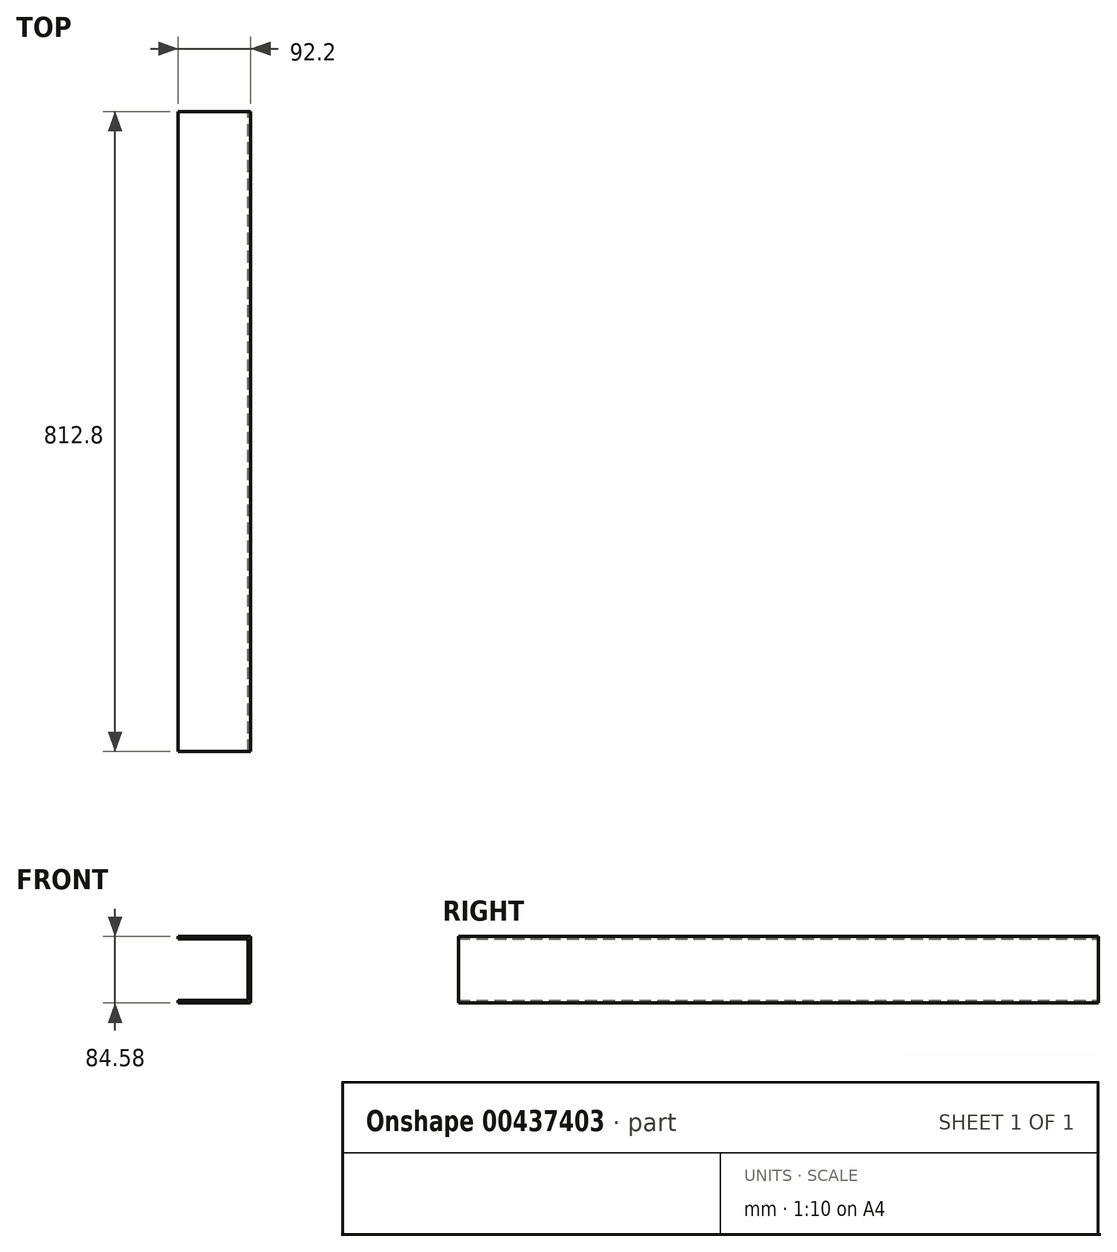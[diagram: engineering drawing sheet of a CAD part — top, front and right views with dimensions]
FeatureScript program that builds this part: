
annotation { "Feature Type Name" : "Feature", "Feature Type Description" : "" }
export const myFeature = defineFeature(function(context is Context, id is Id, definition is map)
    precondition{}
    {
        {
            var Q0;
            Q0=qCreatedBy(makeId("Right.planeOp"),FACE);
            cPlane(context, id + "F0", {"entities" : qUnion([Q0]), "cplaneType" : CPlaneType.OFFSET, "offset" : 457.2 * mm, "width" : 152.4 * mm, "height" : 152.4 * mm});
        }
        {
            var Q0;
            Q0=qCreatedBy(makeId("Front.planeOp"),FACE);
            var sketch = newSketch(context, id + "F1", { "sketchPlane" : qUnion([Q0])});
            skLineSegment(sketch, "E0", {"start": v(263.4, 52.83) * mm, "end": v(355.6, 52.83) * mm});
            skLineSegment(sketch, "E1", {"start": v(355.6, 52.83) * mm, "end": v(355.6, 137.41) * mm});
            skLineSegment(sketch, "E2", {"start": v(355.6, 137.41) * mm, "end": v(263.4, 137.41) * mm});
            skLineSegment(sketch, "E3", {"start": v(263.4, 137.41) * mm, "end": v(263.4, 134.11) * mm});
            skLineSegment(sketch, "E4", {"start": v(263.4, 134.11) * mm, "end": v(352.3, 134.11) * mm});
            skLineSegment(sketch, "E5", {"start": v(352.3, 134.11) * mm, "end": v(352.3, 56.13) * mm});
            skLineSegment(sketch, "E6", {"start": v(352.3, 56.13) * mm, "end": v(263.4, 56.13) * mm});
            skLineSegment(sketch, "E7", {"start": v(263.4, 56.13) * mm, "end": v(263.4, 52.83) * mm});
            skSolve(sketch);
        }
        {
            var Q0;
            Q0 = qSketchRegion(id + "F1", true);
            extrude(context, id + "F2", {"entities" : qUnion([Q0]), "endBound" : BoundingType.SYMMETRIC, "depth" : 812.8 * mm});
        }
    });
